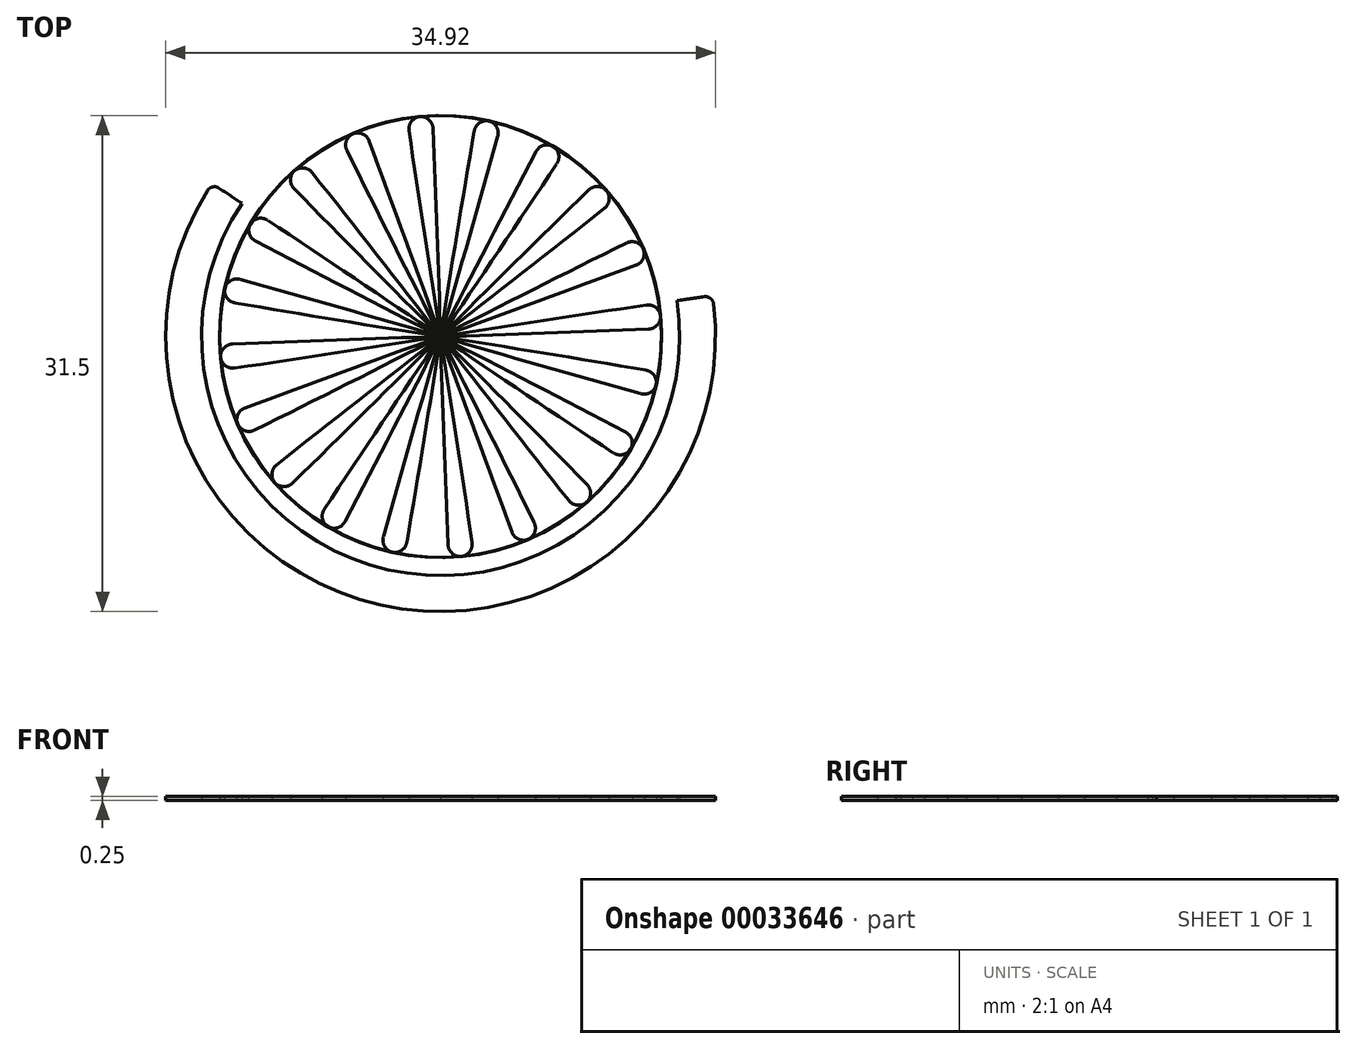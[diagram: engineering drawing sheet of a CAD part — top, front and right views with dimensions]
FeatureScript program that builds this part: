
annotation { "Feature Type Name" : "Feature", "Feature Type Description" : "" }
export const myFeature = defineFeature(function(context is Context, id is Id, definition is map)
    precondition{}
    {
        {
            assignVariable(context, id + "F0", {"name" : "N", "anyValue" : 1.25 * 16});
        }
        {
            assignVariable(context, id + "F1", {"name" : "Swid", "anyValue" : 0.25});
        }
        {
            var Q0;
            Q0=qCreatedBy(makeId("Top.planeOp"),FACE);
            var sketch = newSketch(context, id + "F2", { "sketchPlane" : qUnion([Q0])});
            skCircle(sketch, "E0", {"center": v(0, 0) * mm, "radius": 15.18 * mm, "construction": true});
            skCircle(sketch, "E1", {"center": v(0, 0) * mm, "radius": 15.88 * mm, "construction": true});
            skCircle(sketch, "E2", {"center": v(0, 0) * mm, "radius": 17.46 * mm});
            skLineSegment(sketch, "E3", {"start": v(0, 0) * mm, "end": v(0, 15.18) * mm, "construction": true});
            skLineSegment(sketch, "E4", {"start": v(0, 0) * mm, "end": v(1, 15.15) * mm, "construction": true});
            skLineSegment(sketch, "E5", {"start": v(0, 0) * mm, "end": v(1.98, 15.05) * mm, "construction": true});
            skLineSegment(sketch, "E6", {"start": v(0, 0) * mm, "end": v(2.96, 14.89) * mm, "construction": true});
            skLineSegment(sketch, "E7", {"start": v(0, 0) * mm, "end": v(3.93, 14.66) * mm, "construction": true});
            skCircle(sketch, "E8", {"center": v(0, 0) * mm, "radius": 14.04 * mm});
            skLineSegment(sketch, "E9", {"start": v(1, 15.15) * mm, "end": v(0, 15.21) * mm, "construction": true});
            skLineSegment(sketch, "E10", {"start": v(1.98, 15.05) * mm, "end": v(0.01, 15.31) * mm, "construction": true});
            skLineSegment(sketch, "E11", {"start": v(2.96, 14.89) * mm, "end": v(0.04, 15.47) * mm, "construction": true});
            skLineSegment(sketch, "E12", {"start": v(3.93, 14.66) * mm, "end": v(0.1, 15.7) * mm, "construction": true});
            skLineSegment(sketch, "E13", {"start": v(0, 0) * mm, "end": v(4.88, 14.38) * mm, "construction": true});
            skLineSegment(sketch, "E14", {"start": v(4.88, 14.38) * mm, "end": v(0.18, 15.97) * mm, "construction": true});
            skLineSegment(sketch, "E15", {"start": v(0, 0) * mm, "end": v(5.8, 14.03) * mm, "construction": true});
            skLineSegment(sketch, "E16", {"start": v(0, 0) * mm, "end": v(6.71, 13.62) * mm, "construction": true});
            skLineSegment(sketch, "E17", {"start": v(0, 0) * mm, "end": v(7.6, 13.15) * mm, "construction": true});
            skLineSegment(sketch, "E18", {"start": v(5.8, 14.03) * mm, "end": v(0.3, 16.3) * mm, "construction": true});
            skLineSegment(sketch, "E19", {"start": v(6.71, 13.62) * mm, "end": v(0.48, 16.7) * mm, "construction": true});
            skLineSegment(sketch, "E20", {"start": v(7.6, 13.15) * mm, "end": v(0.7, 17.12) * mm, "construction": true});
            skLineSegment(sketch, "E21", {"start": v(0, 0) * mm, "end": v(8.43, 12.62) * mm, "construction": true});
            skLineSegment(sketch, "E22", {"start": v(0, 0) * mm, "end": v(9.24, 12.04) * mm, "construction": true});
            skLineSegment(sketch, "E23", {"start": v(0, 0) * mm, "end": v(10, 11.41) * mm, "construction": true});
            skLineSegment(sketch, "E24", {"start": v(0, 0) * mm, "end": v(10.73, 10.73) * mm, "construction": true});
            skLineSegment(sketch, "E25", {"start": v(0, 0) * mm, "end": v(11.41, 10) * mm, "construction": true});
            skLineSegment(sketch, "E26", {"start": v(8.43, 12.62) * mm, "end": v(1, 17.6) * mm, "construction": true});
            skLineSegment(sketch, "E27", {"start": v(9.24, 12.04) * mm, "end": v(1.36, 18.1) * mm, "construction": true});
            skLineSegment(sketch, "E28", {"start": v(10, 11.41) * mm, "end": v(1.8, 18.62) * mm, "construction": true});
            skLineSegment(sketch, "E29", {"start": v(10.73, 10.73) * mm, "end": v(2.3, 19.17) * mm, "construction": true});
            skLineSegment(sketch, "E30", {"start": v(11.41, 10) * mm, "end": v(2.9, 19.72) * mm, "construction": true});
            skLineSegment(sketch, "E31", {"start": v(0, 0) * mm, "end": v(12.04, 9.24) * mm, "construction": true});
            skLineSegment(sketch, "E32", {"start": v(12.04, 9.24) * mm, "end": v(3.58, 20.28) * mm, "construction": true});
            skLineSegment(sketch, "E33", {"start": v(0, 0) * mm, "end": v(12.62, 8.43) * mm, "construction": true});
            skLineSegment(sketch, "E34", {"start": v(12.62, 8.43) * mm, "end": v(4.34, 20.83) * mm, "construction": true});
            skSolve(sketch);
        }
        {
            var Q0;
            Q0=qCreatedBy(makeId("Top.planeOp"),FACE);
            var sketch = newSketch(context, id + "F3", { "sketchPlane" : qUnion([Q0])});
            skLineSegment(sketch, "E35.0", {"start": v(12.04, 9.24) * mm, "end": v(3.58, 20.28) * mm, "construction": true});
            skLineSegment(sketch, "E35.1", {"start": v(11.41, 10) * mm, "end": v(2.9, 19.72) * mm, "construction": true});
            skLineSegment(sketch, "E35.2", {"start": v(10.73, 10.73) * mm, "end": v(2.3, 19.17) * mm, "construction": true});
            skLineSegment(sketch, "E35.3", {"start": v(10, 11.41) * mm, "end": v(1.8, 18.62) * mm, "construction": true});
            skLineSegment(sketch, "E35.4", {"start": v(9.24, 12.04) * mm, "end": v(1.36, 18.1) * mm, "construction": true});
            skLineSegment(sketch, "E35.5", {"start": v(8.43, 12.62) * mm, "end": v(1, 17.6) * mm, "construction": true});
            skLineSegment(sketch, "E35.6", {"start": v(7.6, 13.15) * mm, "end": v(0.7, 17.12) * mm, "construction": true});
            skLineSegment(sketch, "E35.7", {"start": v(6.71, 13.62) * mm, "end": v(0.48, 16.7) * mm, "construction": true});
            skLineSegment(sketch, "E35.8", {"start": v(5.8, 14.03) * mm, "end": v(0.3, 16.3) * mm, "construction": true});
            skLineSegment(sketch, "E35.9", {"start": v(4.88, 14.38) * mm, "end": v(0.18, 15.97) * mm, "construction": true});
            skLineSegment(sketch, "E35.10", {"start": v(3.93, 14.66) * mm, "end": v(0.1, 15.7) * mm, "construction": true});
            skLineSegment(sketch, "E35.11", {"start": v(2.96, 14.89) * mm, "end": v(0.04, 15.47) * mm, "construction": true});
            skLineSegment(sketch, "E35.12", {"start": v(1.98, 15.05) * mm, "end": v(0.01, 15.31) * mm, "construction": true});
            skLineSegment(sketch, "E35.13", {"start": v(1, 15.15) * mm, "end": v(0, 15.21) * mm, "construction": true});
            skCircle(sketch, "E35.14", {"center": v(0, 0) * mm, "radius": 15.18 * mm});
            skCircle(sketch, "E35.15", {"center": v(0, 0) * mm, "radius": 14.04 * mm});
            skCircle(sketch, "E35.16", {"center": v(0, 0) * mm, "radius": 15.88 * mm, "construction": true});
            skCircle(sketch, "E35.17", {"center": v(0, 0) * mm, "radius": 17.46 * mm});
            skLineSegment(sketch, "E36.0", {"start": v(12.62, 8.43) * mm, "end": v(4.34, 20.83) * mm, "construction": true});
            skLineSegment(sketch, "E37.0", {"start": v(0, 0) * mm, "end": v(0, 15.18) * mm, "construction": true});
            skFitSpline(sketch, "E38", {"points": [v(0, 20.8) * mm, v(0.04, 21.12) * mm, v(0.3, 22.04) * mm, v(0.97, 23.47) * mm, v(2.25, 25.28) * mm, v(4.27, 27.28) * mm, v(7.12, 29.27) * mm, v(10.86, 31) * mm, v(15.45, 32.22) * mm, v(20.8, 32.68) * mm, v(26.8, 32.15) * mm, v(33.21, 30.42) * mm, v(39.8, 27.34) * mm, v(46.28, 22.79) * mm, v(52.32, 16.74) * mm, v(57.58, 9.22) * mm, v(0, 0) * mm], "startDerivative": vector(7.54, 64.54) * mm, "endDerivative": vector(-870.75, -139.39) * mm});
            skLineSegment(sketch, "E39", {"start": v(2.27, 25.3) * mm, "end": v(0, 0) * mm, "construction": true});
            skLineSegment(sketch, "E40", {"start": v(0, 0) * mm, "end": v(6.47, 28.92) * mm, "construction": true});
            skFitSpline(sketch, "E41.MirrorCS", {"points": [v(8.87, 18.82) * mm, v(8.97, 19.12) * mm, v(9.13, 20.06) * mm, v(9.13, 21.64) * mm, v(8.74, 23.82) * mm, v(7.77, 26.5) * mm, v(6.04, 29.52) * mm, v(3.4, 32.67) * mm, v(-0.23, 35.73) * mm, v(-4.89, 38.43) * mm, v(-10.53, 40.5) * mm, v(-17.07, 41.68) * mm, v(-24.35, 41.7) * mm, v(-32.15, 40.35) * mm, v(-40.19, 37.45) * mm, v(-48.15, 32.89) * mm, v(0, 0) * mm], "startDerivative": vector(20.7, 61.6) * mm, "endDerivative": vector(728.2, -497.34) * mm});
            skLineSegment(sketch, "E42", {"start": v(8.87, 18.82) * mm, "end": v(8.74, 18.55) * mm});
            skLineSegment(sketch, "E43", {"start": v(0, 20.81) * mm, "end": v(0, 20.5) * mm});
            skSolve(sketch);
        }
        {
            var Q0;
            {var subQ3=sQuery(id+"F3.wireOp",EDGE,"E41.MirrorCS");var subQ6=sQuery(id+"F3.wireOp",EDGE,"E35.17");var subQ8=makeQuery(id+"F3.imprint","INTERSECT",VERTEX,{"disambiguationData":[OD(1.0)],"derivedFrom":[subQ6,subQ3]});Q0=makeQuery(id+"F3.imprint","IMPRINT",FACE,{"disambiguationData":[TD([[makeQuery(id+"F3.imprint","IMPRINT",EDGE,{"disambiguationData":[TD([[subQ8,-1.0]])],"derivedFrom":subQ6}),1.0]])]});}
            var Q1;
            {var subQ3=sQuery(id+"F3.wireOp",EDGE,"E41.MirrorCS");var subQ5=sQuery(id+"F3.wireOp",EDGE,"E35.15");var subQ6=makeQuery(id+"F3.imprint","INTERSECT",VERTEX,{"derivedFrom":[subQ5,subQ3]});Q1=makeQuery(id+"F3.imprint","IMPRINT",FACE,{"disambiguationData":[TD([[makeQuery(id+"F3.imprint","IMPRINT",EDGE,{"disambiguationData":[TD([[subQ6,-1.0]])],"derivedFrom":subQ5}),1.0]])]});}
            var Q2;
            {var subQ2=sQuery(id+"F3.wireOp",EDGE,"E42");Q2=makeQuery(id+"F3.imprint","IMPRINT",FACE,{"disambiguationData":[TD([[makeQuery(id+"F3.imprint","IMPRINT",EDGE,{"derivedFrom":subQ2}),-1.0]])]});}
            extrude(context, id + "F4", {"entities" : qUnion([Q0, Q1, Q2]), "depth" : (getVariable(context, 'Swid')) * mm, "offsetDistance" : 25.4 * mm});
        }
        {
            var Q0;
            Q0=qCreatedBy(makeId("Right.planeOp"),FACE);
            var sketch = newSketch(context, id + "F5", { "sketchPlane" : qUnion([Q0])});
            skLineSegment(sketch, "E44", {"start": v(0, 0) * mm, "end": v(0, 43.3) * mm, "construction": true});
            skSolve(sketch);
        }
        {
            var Q0;
            Q0=makeQuery(id+"F4.opExtrude","SWEPT_EDGE",EDGE,{"disambiguationData":[OSD([sQuery(id+"F3.wireOp",EDGE,"E35.17"),sQuery(id+"F3.wireOp",EDGE,"E41.MirrorCS")])]});
            var Q1;
            Q1=makeQuery(id+"F4.opExtrude","SWEPT_EDGE",EDGE,{"disambiguationData":[OSD([sQuery(id+"F3.wireOp",EDGE,"E35.17"),sQuery(id+"F3.wireOp",EDGE,"E38")])]});
            fillet(context, id + "F6", {"entities" : qUnion([Q0, Q1]), "radius" : 0.5 * mm, "tangentPropagation" : true, "allowEdgeOverflow" : false});
        }
        {
            var Q0;
            Q0=makeQuery(id+"F4.opExtrude","SWEPT_EDGE",EDGE,{"disambiguationData":[OSD([sQuery(id+"F3.wireOp",EDGE,"E35.15"),sQuery(id+"F3.wireOp",EDGE,"E42")])]});
            var Q1;
            Q1=makeQuery(id+"F4.opExtrude","SWEPT_EDGE",EDGE,{"disambiguationData":[OSD([sQuery(id+"F3.wireOp",EDGE,"E35.15"),sQuery(id+"F3.wireOp",EDGE,"E43")])]});
            fillet(context, id + "F7", {"entities" : qUnion([Q0, Q1]), "radius" : 0.8 * mm, "tangentPropagation" : true, "allowEdgeOverflow" : false});
        }
        {
            var Q0;
            Q0=makeQuery(id+"F4.opExtrude","SWEPT_BODY",BODY,{"disambiguationData":[OSD([sQuery(id+"F3.wireOp",EDGE,"E35.15"),sQuery(id+"F3.wireOp",EDGE,"E35.17"),sQuery(id+"F3.wireOp",EDGE,"E38"),sQuery(id+"F3.wireOp",EDGE,"E41.MirrorCS"),sQuery(id+"F3.wireOp",EDGE,"9305e2c8-a00a-4cbc-a3b2-8fc88bc1717c"),sQuery(id+"F3.wireOp",EDGE,"f762f43d-eaf9-45ff-b6cd-062fd530227c")])]});
            var Q1;
            Q1=sQuery(id+"F5.wireOp",EDGE,"E44");
            circularPattern(context, id + "F8", {"operationType" : NewBodyOperationType.ADD, "entities" : qUnion([Q0]), "axis" : qUnion([Q1]), "angle" : (360 / getVariable(context, 'N')) * degree, "instanceCount" : getVariable(context, 'N'), "oppositeDirection" : true});
        }
    });
